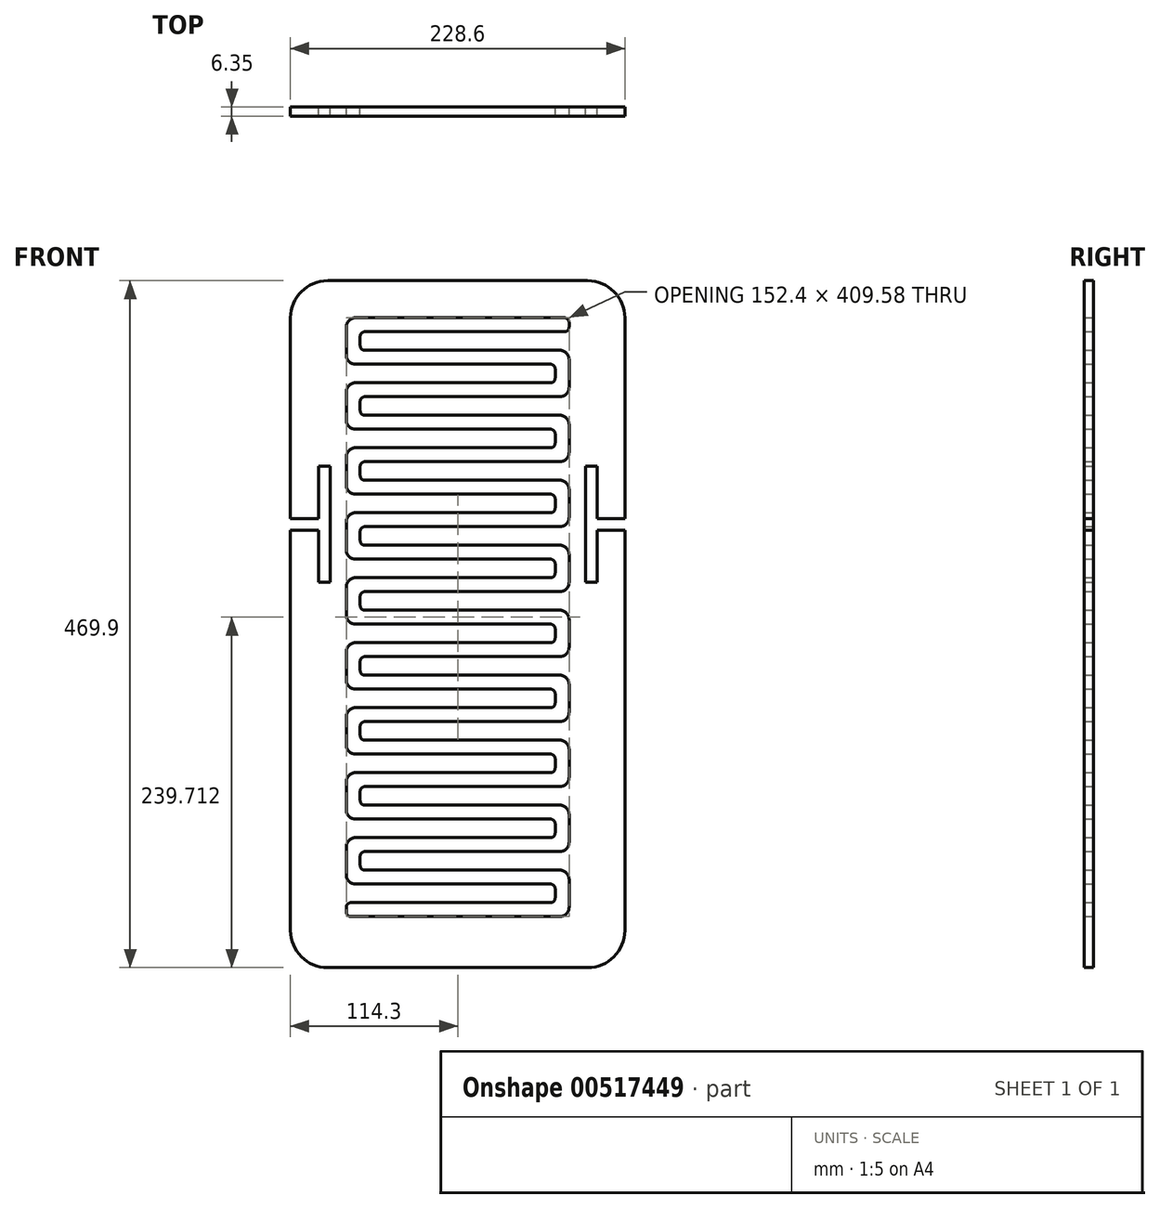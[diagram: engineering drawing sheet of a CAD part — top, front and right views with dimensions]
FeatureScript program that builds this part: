
annotation { "Feature Type Name" : "Feature", "Feature Type Description" : "" }
export const myFeature = defineFeature(function(context is Context, id is Id, definition is map)
    precondition{}
    {
        {
            var Q0;
            Q0=qCreatedBy(makeId("Front.planeOp"),FACE);
            var sketch = newSketch(context, id + "F0", { "sketchPlane" : qUnion([Q0])});
            skLineSegment(sketch, "E0.bottom", {"start": v(88.9, -234.95) * mm, "end": v(-88.9, -234.95) * mm});
            skLineSegment(sketch, "E0.top", {"start": v(88.9, 234.95) * mm, "end": v(-88.9, 234.95) * mm});
            skLineSegment(sketch, "E0.left", {"start": v(114.3, -209.55) * mm, "end": v(114.3, 209.55) * mm});
            skLineSegment(sketch, "E0.right", {"start": v(-114.3, -209.55) * mm, "end": v(-114.3, 209.55) * mm});
            skPoint(sketch, "E0.middle", {"position": v(0, 0) * mm});
            skPoint(sketch, "E1.visualSharp", {"position": v(-114.3, 234.95) * mm});
            skArc(sketch, "E1.filletArc", {"start": v(-88.9, 234.95) * mm, "mid": v(-106.86, 227.51) * mm, "end": v(-114.3, 209.55) * mm});
            skPoint(sketch, "E2.visualSharp", {"position": v(114.3, 234.95) * mm});
            skArc(sketch, "E2.filletArc", {"start": v(114.3, 209.55) * mm, "mid": v(106.86, 227.51) * mm, "end": v(88.9, 234.95) * mm});
            skPoint(sketch, "E3.visualSharp", {"position": v(114.3, -234.95) * mm});
            skArc(sketch, "E3.filletArc", {"start": v(88.9, -234.95) * mm, "mid": v(106.86, -227.51) * mm, "end": v(114.3, -209.55) * mm});
            skPoint(sketch, "E4.visualSharp", {"position": v(-114.3, -234.95) * mm});
            skArc(sketch, "E4.filletArc", {"start": v(-114.3, -209.55) * mm, "mid": v(-106.86, -227.51) * mm, "end": v(-88.9, -234.95) * mm});
            skLineSegment(sketch, "E5.bottom", {"start": v(-95.25, 107.95) * mm, "end": v(-87.31, 107.95) * mm});
            skLineSegment(sketch, "E5.top", {"start": v(-95.25, 28.57) * mm, "end": v(-87.31, 28.57) * mm});
            skLineSegment(sketch, "E5.left", {"start": v(-95.25, 107.95) * mm, "end": v(-95.25, 28.57) * mm});
            skLineSegment(sketch, "E5.right", {"start": v(-87.31, 107.95) * mm, "end": v(-87.31, 28.57) * mm});
            skLineSegment(sketch, "E6.MirrorCS", {"start": v(95.25, 107.95) * mm, "end": v(87.31, 107.95) * mm});
            skLineSegment(sketch, "E7.MirrorCS", {"start": v(95.25, 28.58) * mm, "end": v(87.31, 28.58) * mm});
            skLineSegment(sketch, "E8.MirrorCS", {"start": v(87.31, 107.95) * mm, "end": v(87.31, 28.57) * mm});
            skLineSegment(sketch, "E9.MirrorCS", {"start": v(95.25, 107.95) * mm, "end": v(95.25, 28.57) * mm});
            skLineSegment(sketch, "E10", {"start": v(-69.85, 209.55) * mm, "end": v(73.02, 209.55) * mm});
            skLineSegment(sketch, "E11", {"start": v(76.2, 206.38) * mm, "end": v(76.2, 203.2) * mm});
            skLineSegment(sketch, "E12", {"start": v(73.02, 200.03) * mm, "end": v(-63.5, 200.03) * mm});
            skLineSegment(sketch, "E13", {"start": v(-66.68, 196.85) * mm, "end": v(-66.68, 190.5) * mm});
            skLineSegment(sketch, "E14", {"start": v(-63.5, 187.33) * mm, "end": v(69.85, 187.33) * mm});
            skLineSegment(sketch, "E15", {"start": v(76.2, 180.98) * mm, "end": v(76.2, 161.93) * mm});
            skLineSegment(sketch, "E16", {"start": v(-76.2, 203.2) * mm, "end": v(-76.2, 184.15) * mm});
            skLineSegment(sketch, "E17", {"start": v(-69.85, 177.8) * mm, "end": v(63.5, 177.8) * mm});
            skLineSegment(sketch, "E18", {"start": v(66.67, 174.63) * mm, "end": v(66.67, 168.28) * mm});
            skLineSegment(sketch, "E19", {"start": v(63.5, 165.1) * mm, "end": v(-69.85, 165.1) * mm});
            skPoint(sketch, "E20.visualSharp", {"position": v(-76.2, 209.55) * mm});
            skArc(sketch, "E20.filletArc", {"start": v(-69.85, 209.55) * mm, "mid": v(-74.34, 207.7) * mm, "end": v(-76.2, 203.2) * mm});
            skPoint(sketch, "E21.visualSharp", {"position": v(-66.68, 200.03) * mm});
            skArc(sketch, "E21.filletArc", {"start": v(-63.5, 200.03) * mm, "mid": v(-65.75, 199.1) * mm, "end": v(-66.68, 196.85) * mm});
            skPoint(sketch, "E22.visualSharp", {"position": v(-66.68, 187.33) * mm});
            skArc(sketch, "E22.filletArc", {"start": v(-66.68, 190.5) * mm, "mid": v(-65.75, 188.25) * mm, "end": v(-63.5, 187.33) * mm});
            skPoint(sketch, "E23.visualSharp", {"position": v(-76.2, 177.8) * mm});
            skArc(sketch, "E23.filletArc", {"start": v(-76.2, 184.15) * mm, "mid": v(-74.34, 179.66) * mm, "end": v(-69.85, 177.8) * mm});
            skPoint(sketch, "E24.visualSharp", {"position": v(76.2, 187.33) * mm});
            skArc(sketch, "E24.filletArc", {"start": v(76.2, 180.98) * mm, "mid": v(74.34, 185.47) * mm, "end": v(69.85, 187.33) * mm});
            skPoint(sketch, "E25.visualSharp", {"position": v(76.2, 200.03) * mm});
            skArc(sketch, "E25.filletArc", {"start": v(73.02, 200.03) * mm, "mid": v(75.27, 200.95) * mm, "end": v(76.2, 203.2) * mm});
            skPoint(sketch, "E26.visualSharp", {"position": v(76.2, 209.55) * mm});
            skArc(sketch, "E26.filletArc", {"start": v(76.2, 206.38) * mm, "mid": v(75.27, 208.62) * mm, "end": v(73.02, 209.55) * mm});
            skPoint(sketch, "E27.visualSharp", {"position": v(66.67, 177.8) * mm});
            skArc(sketch, "E27.filletArc", {"start": v(66.67, 174.63) * mm, "mid": v(65.75, 176.87) * mm, "end": v(63.5, 177.8) * mm});
            skPoint(sketch, "E28.visualSharp", {"position": v(66.67, 165.1) * mm});
            skArc(sketch, "E28.filletArc", {"start": v(63.5, 165.1) * mm, "mid": v(65.75, 166.03) * mm, "end": v(66.67, 168.28) * mm});
            skArc(sketch, "E29.filletArc", {"start": v(69.85, 155.58) * mm, "mid": v(74.34, 157.43) * mm, "end": v(76.2, 161.93) * mm});
            skPoint(sketch, "E30.visualSharp", {"position": v(-76.2, 165.1) * mm});
            skLineSegment(sketch, "E31", {"start": v(69.85, 155.58) * mm, "end": v(-63.5, 155.58) * mm});
            skLineSegment(sketch, "E32.0.1.0", {"start": v(69.85, 111.13) * mm, "end": v(-63.5, 111.13) * mm});
            skLineSegment(sketch, "E32.0.1.1", {"start": v(63.5, 120.65) * mm, "end": v(-69.85, 120.65) * mm});
            skArc(sketch, "E32.0.1.2", {"start": v(69.85, 111.13) * mm, "mid": v(74.34, 112.98) * mm, "end": v(76.2, 117.48) * mm});
            skLineSegment(sketch, "E32.0.1.3", {"start": v(76.2, 136.53) * mm, "end": v(76.2, 117.48) * mm});
            skArc(sketch, "E32.0.1.4", {"start": v(63.5, 120.65) * mm, "mid": v(65.75, 121.58) * mm, "end": v(66.67, 123.83) * mm});
            skLineSegment(sketch, "E32.0.1.5", {"start": v(66.67, 130.18) * mm, "end": v(66.67, 123.83) * mm});
            skArc(sketch, "E32.0.1.6", {"start": v(66.67, 130.18) * mm, "mid": v(65.75, 132.42) * mm, "end": v(63.5, 133.35) * mm});
            skArc(sketch, "E32.0.1.7", {"start": v(76.2, 136.53) * mm, "mid": v(74.34, 141.02) * mm, "end": v(69.85, 142.88) * mm});
            skLineSegment(sketch, "E32.0.1.8", {"start": v(-63.5, 142.88) * mm, "end": v(69.85, 142.88) * mm});
            skLineSegment(sketch, "E32.0.1.9", {"start": v(-69.85, 133.35) * mm, "end": v(63.5, 133.35) * mm});
            skArc(sketch, "E32.0.1.10", {"start": v(-76.2, 139.7) * mm, "mid": v(-74.34, 135.2) * mm, "end": v(-69.85, 133.35) * mm});
            skLineSegment(sketch, "E32.0.1.11", {"start": v(-76.2, 158.75) * mm, "end": v(-76.2, 139.7) * mm});
            skArc(sketch, "E32.0.1.12", {"start": v(-69.85, 165.1) * mm, "mid": v(-74.34, 163.24) * mm, "end": v(-76.2, 158.75) * mm});
            skArc(sketch, "E32.0.1.13", {"start": v(-63.5, 155.57) * mm, "mid": v(-65.75, 154.65) * mm, "end": v(-66.68, 152.4) * mm});
            skLineSegment(sketch, "E32.0.1.14", {"start": v(-66.68, 152.4) * mm, "end": v(-66.68, 146.05) * mm});
            skArc(sketch, "E32.0.1.15", {"start": v(-66.68, 146.05) * mm, "mid": v(-65.75, 143.8) * mm, "end": v(-63.5, 142.88) * mm});
            skLineSegment(sketch, "E32.direction1", {"start": v(-63.5, 155.58) * mm, "end": v(-38.1, 155.58) * mm, "construction": true});
            skLineSegment(sketch, "E32.direction2", {"start": v(-63.5, 155.58) * mm, "end": v(-63.5, 111.13) * mm, "construction": true});
            skLineSegment(sketch, "E33.0.0.2", {"start": v(69.85, 66.68) * mm, "end": v(-63.5, 66.68) * mm});
            skLineSegment(sketch, "E33.3.0.2", {"start": v(63.5, 76.2) * mm, "end": v(-69.85, 76.2) * mm});
            skArc(sketch, "E33.6.0.2", {"start": v(69.85, 66.68) * mm, "mid": v(74.34, 68.53) * mm, "end": v(76.2, 73.03) * mm});
            skLineSegment(sketch, "E33.10.0.2", {"start": v(76.2, 92.08) * mm, "end": v(76.2, 73.03) * mm});
            skArc(sketch, "E33.13.0.2", {"start": v(63.5, 76.2) * mm, "mid": v(65.75, 77.13) * mm, "end": v(66.67, 79.38) * mm});
            skLineSegment(sketch, "E33.17.0.2", {"start": v(66.67, 85.73) * mm, "end": v(66.67, 79.38) * mm});
            skArc(sketch, "E33.20.0.2", {"start": v(66.67, 85.73) * mm, "mid": v(65.75, 87.97) * mm, "end": v(63.5, 88.9) * mm});
            skArc(sketch, "E33.24.0.2", {"start": v(76.2, 92.08) * mm, "mid": v(74.34, 96.57) * mm, "end": v(69.85, 98.43) * mm});
            skLineSegment(sketch, "E33.28.0.2", {"start": v(-63.5, 98.43) * mm, "end": v(69.85, 98.43) * mm});
            skLineSegment(sketch, "E33.31.0.2", {"start": v(-69.85, 88.9) * mm, "end": v(63.5, 88.9) * mm});
            skArc(sketch, "E33.34.0.2", {"start": v(-76.2, 95.25) * mm, "mid": v(-74.34, 90.76) * mm, "end": v(-69.85, 88.9) * mm});
            skLineSegment(sketch, "E33.38.0.2", {"start": v(-76.2, 114.3) * mm, "end": v(-76.2, 95.25) * mm});
            skArc(sketch, "E33.41.0.2", {"start": v(-69.85, 120.65) * mm, "mid": v(-74.34, 118.8) * mm, "end": v(-76.2, 114.3) * mm});
            skArc(sketch, "E33.45.0.2", {"start": v(-63.5, 111.12) * mm, "mid": v(-65.75, 110.2) * mm, "end": v(-66.68, 107.95) * mm});
            skLineSegment(sketch, "E33.49.0.2", {"start": v(-66.68, 107.95) * mm, "end": v(-66.68, 101.6) * mm});
            skArc(sketch, "E33.52.0.2", {"start": v(-66.68, 101.6) * mm, "mid": v(-65.75, 99.35) * mm, "end": v(-63.5, 98.43) * mm});
            skLineSegment(sketch, "E33.0.0.3", {"start": v(69.85, 22.23) * mm, "end": v(-63.5, 22.23) * mm});
            skLineSegment(sketch, "E33.3.0.3", {"start": v(63.5, 31.75) * mm, "end": v(-69.85, 31.75) * mm});
            skArc(sketch, "E33.6.0.3", {"start": v(69.85, 22.23) * mm, "mid": v(74.34, 24.08) * mm, "end": v(76.2, 28.58) * mm});
            skLineSegment(sketch, "E33.10.0.3", {"start": v(76.2, 47.63) * mm, "end": v(76.2, 28.58) * mm});
            skArc(sketch, "E33.13.0.3", {"start": v(63.5, 31.75) * mm, "mid": v(65.75, 32.68) * mm, "end": v(66.67, 34.93) * mm});
            skLineSegment(sketch, "E33.17.0.3", {"start": v(66.67, 41.28) * mm, "end": v(66.67, 34.93) * mm});
            skArc(sketch, "E33.20.0.3", {"start": v(66.67, 41.28) * mm, "mid": v(65.75, 43.52) * mm, "end": v(63.5, 44.45) * mm});
            skArc(sketch, "E33.24.0.3", {"start": v(76.2, 47.63) * mm, "mid": v(74.34, 52.12) * mm, "end": v(69.85, 53.98) * mm});
            skLineSegment(sketch, "E33.28.0.3", {"start": v(-63.5, 53.98) * mm, "end": v(69.85, 53.98) * mm});
            skLineSegment(sketch, "E33.31.0.3", {"start": v(-69.85, 44.45) * mm, "end": v(63.5, 44.45) * mm});
            skArc(sketch, "E33.34.0.3", {"start": v(-76.2, 50.8) * mm, "mid": v(-74.34, 46.3) * mm, "end": v(-69.85, 44.45) * mm});
            skLineSegment(sketch, "E33.38.0.3", {"start": v(-76.2, 69.85) * mm, "end": v(-76.2, 50.8) * mm});
            skArc(sketch, "E33.41.0.3", {"start": v(-69.85, 76.2) * mm, "mid": v(-74.34, 74.34) * mm, "end": v(-76.2, 69.85) * mm});
            skArc(sketch, "E33.45.0.3", {"start": v(-63.5, 66.67) * mm, "mid": v(-65.75, 65.75) * mm, "end": v(-66.68, 63.5) * mm});
            skLineSegment(sketch, "E33.49.0.3", {"start": v(-66.68, 63.5) * mm, "end": v(-66.68, 57.15) * mm});
            skArc(sketch, "E33.52.0.3", {"start": v(-66.68, 57.15) * mm, "mid": v(-65.75, 54.9) * mm, "end": v(-63.5, 53.98) * mm});
            skLineSegment(sketch, "E33.0.0.4", {"start": v(69.85, -22.22) * mm, "end": v(-63.5, -22.22) * mm});
            skLineSegment(sketch, "E33.3.0.4", {"start": v(63.5, -12.7) * mm, "end": v(-69.85, -12.7) * mm});
            skArc(sketch, "E33.6.0.4", {"start": v(69.85, -22.22) * mm, "mid": v(74.34, -20.37) * mm, "end": v(76.2, -15.87) * mm});
            skLineSegment(sketch, "E33.10.0.4", {"start": v(76.2, 3.18) * mm, "end": v(76.2, -15.87) * mm});
            skArc(sketch, "E33.13.0.4", {"start": v(63.5, -12.7) * mm, "mid": v(65.75, -11.77) * mm, "end": v(66.67, -9.52) * mm});
            skLineSegment(sketch, "E33.17.0.4", {"start": v(66.67, -3.17) * mm, "end": v(66.67, -9.52) * mm});
            skArc(sketch, "E33.20.0.4", {"start": v(66.67, -3.17) * mm, "mid": v(65.75, -0.93) * mm, "end": v(63.5, 0) * mm});
            skArc(sketch, "E33.24.0.4", {"start": v(76.2, 3.18) * mm, "mid": v(74.34, 7.67) * mm, "end": v(69.85, 9.53) * mm});
            skLineSegment(sketch, "E33.28.0.4", {"start": v(-63.5, 9.53) * mm, "end": v(69.85, 9.53) * mm});
            skLineSegment(sketch, "E33.31.0.4", {"start": v(-69.85, 0) * mm, "end": v(63.5, 0) * mm});
            skArc(sketch, "E33.34.0.4", {"start": v(-76.2, 6.35) * mm, "mid": v(-74.34, 1.86) * mm, "end": v(-69.85, 0) * mm});
            skLineSegment(sketch, "E33.38.0.4", {"start": v(-76.2, 25.4) * mm, "end": v(-76.2, 6.35) * mm});
            skArc(sketch, "E33.41.0.4", {"start": v(-69.85, 31.75) * mm, "mid": v(-74.34, 29.9) * mm, "end": v(-76.2, 25.4) * mm});
            skArc(sketch, "E33.45.0.4", {"start": v(-63.5, 22.22) * mm, "mid": v(-65.75, 21.3) * mm, "end": v(-66.68, 19.05) * mm});
            skLineSegment(sketch, "E33.49.0.4", {"start": v(-66.68, 19.05) * mm, "end": v(-66.68, 12.7) * mm});
            skArc(sketch, "E33.52.0.4", {"start": v(-66.68, 12.7) * mm, "mid": v(-65.75, 10.45) * mm, "end": v(-63.5, 9.53) * mm});
            skLineSegment(sketch, "E33.0.0.5", {"start": v(69.85, -66.67) * mm, "end": v(-63.5, -66.67) * mm});
            skLineSegment(sketch, "E33.3.0.5", {"start": v(63.5, -57.15) * mm, "end": v(-69.85, -57.15) * mm});
            skArc(sketch, "E33.6.0.5", {"start": v(69.85, -66.67) * mm, "mid": v(74.34, -64.82) * mm, "end": v(76.2, -60.32) * mm});
            skLineSegment(sketch, "E33.10.0.5", {"start": v(76.2, -41.27) * mm, "end": v(76.2, -60.32) * mm});
            skArc(sketch, "E33.13.0.5", {"start": v(63.5, -57.15) * mm, "mid": v(65.75, -56.22) * mm, "end": v(66.67, -53.97) * mm});
            skLineSegment(sketch, "E33.17.0.5", {"start": v(66.67, -47.62) * mm, "end": v(66.67, -53.97) * mm});
            skArc(sketch, "E33.20.0.5", {"start": v(66.67, -47.62) * mm, "mid": v(65.75, -45.38) * mm, "end": v(63.5, -44.45) * mm});
            skArc(sketch, "E33.24.0.5", {"start": v(76.2, -41.27) * mm, "mid": v(74.34, -36.78) * mm, "end": v(69.85, -34.92) * mm});
            skLineSegment(sketch, "E33.28.0.5", {"start": v(-63.5, -34.92) * mm, "end": v(69.85, -34.92) * mm});
            skLineSegment(sketch, "E33.31.0.5", {"start": v(-69.85, -44.45) * mm, "end": v(63.5, -44.45) * mm});
            skArc(sketch, "E33.34.0.5", {"start": v(-76.2, -38.1) * mm, "mid": v(-74.34, -42.6) * mm, "end": v(-69.85, -44.45) * mm});
            skLineSegment(sketch, "E33.38.0.5", {"start": v(-76.2, -19.05) * mm, "end": v(-76.2, -38.1) * mm});
            skArc(sketch, "E33.41.0.5", {"start": v(-69.85, -12.7) * mm, "mid": v(-74.34, -14.56) * mm, "end": v(-76.2, -19.05) * mm});
            skArc(sketch, "E33.45.0.5", {"start": v(-63.5, -22.23) * mm, "mid": v(-65.75, -23.15) * mm, "end": v(-66.68, -25.4) * mm});
            skLineSegment(sketch, "E33.49.0.5", {"start": v(-66.68, -25.4) * mm, "end": v(-66.68, -31.75) * mm});
            skArc(sketch, "E33.52.0.5", {"start": v(-66.68, -31.75) * mm, "mid": v(-65.75, -34) * mm, "end": v(-63.5, -34.92) * mm});
            skLineSegment(sketch, "E33.0.0.6", {"start": v(69.85, -111.12) * mm, "end": v(-63.5, -111.12) * mm});
            skLineSegment(sketch, "E33.3.0.6", {"start": v(63.5, -101.6) * mm, "end": v(-69.85, -101.6) * mm});
            skArc(sketch, "E33.6.0.6", {"start": v(69.85, -111.12) * mm, "mid": v(74.34, -109.27) * mm, "end": v(76.2, -104.77) * mm});
            skLineSegment(sketch, "E33.10.0.6", {"start": v(76.2, -85.72) * mm, "end": v(76.2, -104.77) * mm});
            skArc(sketch, "E33.13.0.6", {"start": v(63.5, -101.6) * mm, "mid": v(65.75, -100.67) * mm, "end": v(66.67, -98.42) * mm});
            skLineSegment(sketch, "E33.17.0.6", {"start": v(66.67, -92.07) * mm, "end": v(66.67, -98.42) * mm});
            skArc(sketch, "E33.20.0.6", {"start": v(66.67, -92.07) * mm, "mid": v(65.75, -89.83) * mm, "end": v(63.5, -88.9) * mm});
            skArc(sketch, "E33.24.0.6", {"start": v(76.2, -85.72) * mm, "mid": v(74.34, -81.23) * mm, "end": v(69.85, -79.37) * mm});
            skLineSegment(sketch, "E33.28.0.6", {"start": v(-63.5, -79.37) * mm, "end": v(69.85, -79.37) * mm});
            skLineSegment(sketch, "E33.31.0.6", {"start": v(-69.85, -88.9) * mm, "end": v(63.5, -88.9) * mm});
            skArc(sketch, "E33.34.0.6", {"start": v(-76.2, -82.55) * mm, "mid": v(-74.34, -87.04) * mm, "end": v(-69.85, -88.9) * mm});
            skLineSegment(sketch, "E33.38.0.6", {"start": v(-76.2, -63.5) * mm, "end": v(-76.2, -82.55) * mm});
            skArc(sketch, "E33.41.0.6", {"start": v(-69.85, -57.15) * mm, "mid": v(-74.34, -59) * mm, "end": v(-76.2, -63.5) * mm});
            skArc(sketch, "E33.45.0.6", {"start": v(-63.5, -66.68) * mm, "mid": v(-65.75, -67.6) * mm, "end": v(-66.68, -69.85) * mm});
            skLineSegment(sketch, "E33.49.0.6", {"start": v(-66.68, -69.85) * mm, "end": v(-66.68, -76.2) * mm});
            skArc(sketch, "E33.52.0.6", {"start": v(-66.68, -76.2) * mm, "mid": v(-65.75, -78.45) * mm, "end": v(-63.5, -79.38) * mm});
            skLineSegment(sketch, "E33.0.0.7", {"start": v(69.85, -155.57) * mm, "end": v(-63.5, -155.57) * mm});
            skLineSegment(sketch, "E33.3.0.7", {"start": v(63.5, -146.05) * mm, "end": v(-69.85, -146.05) * mm});
            skArc(sketch, "E33.6.0.7", {"start": v(69.85, -155.57) * mm, "mid": v(74.34, -153.72) * mm, "end": v(76.2, -149.22) * mm});
            skLineSegment(sketch, "E33.10.0.7", {"start": v(76.2, -130.17) * mm, "end": v(76.2, -149.22) * mm});
            skArc(sketch, "E33.13.0.7", {"start": v(63.5, -146.05) * mm, "mid": v(65.75, -145.12) * mm, "end": v(66.67, -142.87) * mm});
            skLineSegment(sketch, "E33.17.0.7", {"start": v(66.67, -136.52) * mm, "end": v(66.67, -142.87) * mm});
            skArc(sketch, "E33.20.0.7", {"start": v(66.67, -136.52) * mm, "mid": v(65.75, -134.28) * mm, "end": v(63.5, -133.35) * mm});
            skArc(sketch, "E33.24.0.7", {"start": v(76.2, -130.17) * mm, "mid": v(74.34, -125.68) * mm, "end": v(69.85, -123.82) * mm});
            skLineSegment(sketch, "E33.28.0.7", {"start": v(-63.5, -123.82) * mm, "end": v(69.85, -123.82) * mm});
            skLineSegment(sketch, "E33.31.0.7", {"start": v(-69.85, -133.35) * mm, "end": v(63.5, -133.35) * mm});
            skArc(sketch, "E33.34.0.7", {"start": v(-76.2, -127) * mm, "mid": v(-74.34, -131.5) * mm, "end": v(-69.85, -133.35) * mm});
            skLineSegment(sketch, "E33.38.0.7", {"start": v(-76.2, -107.95) * mm, "end": v(-76.2, -127) * mm});
            skArc(sketch, "E33.41.0.7", {"start": v(-69.85, -101.6) * mm, "mid": v(-74.34, -103.46) * mm, "end": v(-76.2, -107.95) * mm});
            skArc(sketch, "E33.45.0.7", {"start": v(-63.5, -111.13) * mm, "mid": v(-65.75, -112.05) * mm, "end": v(-66.68, -114.3) * mm});
            skLineSegment(sketch, "E33.49.0.7", {"start": v(-66.68, -114.3) * mm, "end": v(-66.68, -120.65) * mm});
            skArc(sketch, "E33.52.0.7", {"start": v(-66.68, -120.65) * mm, "mid": v(-65.75, -122.9) * mm, "end": v(-63.5, -123.83) * mm});
            skPoint(sketch, "E34.visualSharp", {"position": v(120.65, -352.42) * mm});
            skArc(sketch, "E34.filletArc", {"start": v(120.65, -355.6) * mm, "mid": v(119.72, -353.35) * mm, "end": v(117.47, -352.42) * mm});
            skPoint(sketch, "E35.visualSharp", {"position": v(120.65, -361.95) * mm});
            skArc(sketch, "E35.filletArc", {"start": v(117.47, -361.95) * mm, "mid": v(119.72, -361.02) * mm, "end": v(120.65, -358.77) * mm});
            skLineSegment(sketch, "E36", {"start": v(-95.25, 68.26) * mm, "end": v(-114.3, 68.26) * mm, "construction": true});
            skLineSegment(sketch, "E37.bottom", {"start": v(-114.3, 72.23) * mm, "end": v(-95.25, 72.23) * mm});
            skLineSegment(sketch, "E37.top", {"start": v(-114.3, 64.3) * mm, "end": v(-95.25, 64.3) * mm});
            skLineSegment(sketch, "E37.left", {"start": v(-114.3, 72.23) * mm, "end": v(-114.3, 64.3) * mm});
            skLineSegment(sketch, "E37.right", {"start": v(-95.25, 72.23) * mm, "end": v(-95.25, 64.3) * mm});
            skLineSegment(sketch, "E38.MirrorCS", {"start": v(-95.25, 64.3) * mm, "end": v(-95.25, 72.23) * mm});
            skLineSegment(sketch, "E39.MirrorCS", {"start": v(-114.3, 64.3) * mm, "end": v(-114.3, 72.23) * mm});
            skLineSegment(sketch, "E40.MirrorCS", {"start": v(114.3, 72.23) * mm, "end": v(114.3, 64.3) * mm});
            skLineSegment(sketch, "E41.MirrorCS", {"start": v(95.25, 72.23) * mm, "end": v(95.25, 64.3) * mm});
            skLineSegment(sketch, "E42.MirrorCS", {"start": v(114.3, 72.23) * mm, "end": v(95.25, 72.23) * mm});
            skLineSegment(sketch, "E43.MirrorCS", {"start": v(114.3, 64.3) * mm, "end": v(95.25, 64.3) * mm});
            skLineSegment(sketch, "E44.MirrorCS", {"start": v(95.25, 64.3) * mm, "end": v(95.25, 72.23) * mm});
            skLineSegment(sketch, "E45.MirrorCS", {"start": v(114.3, 64.3) * mm, "end": v(114.3, 72.23) * mm});
            skLineSegment(sketch, "E46.MirrorCS", {"start": v(95.25, 68.26) * mm, "end": v(114.3, 68.26) * mm, "construction": true});
            skLineSegment(sketch, "E47.0.0.8", {"start": v(69.85, -200.02) * mm, "end": v(-63.5, -200.02) * mm});
            skLineSegment(sketch, "E47.3.0.8", {"start": v(63.5, -190.5) * mm, "end": v(-69.85, -190.5) * mm});
            skArc(sketch, "E47.6.0.8", {"start": v(69.85, -200.02) * mm, "mid": v(74.34, -198.17) * mm, "end": v(76.2, -193.67) * mm});
            skLineSegment(sketch, "E47.10.0.8", {"start": v(76.2, -174.62) * mm, "end": v(76.2, -193.67) * mm});
            skArc(sketch, "E47.13.0.8", {"start": v(63.5, -190.5) * mm, "mid": v(65.75, -189.57) * mm, "end": v(66.67, -187.32) * mm});
            skLineSegment(sketch, "E47.17.0.8", {"start": v(66.67, -180.97) * mm, "end": v(66.67, -187.32) * mm});
            skArc(sketch, "E47.20.0.8", {"start": v(66.67, -180.97) * mm, "mid": v(65.75, -178.73) * mm, "end": v(63.5, -177.8) * mm});
            skArc(sketch, "E47.24.0.8", {"start": v(76.2, -174.62) * mm, "mid": v(74.34, -170.13) * mm, "end": v(69.85, -168.27) * mm});
            skLineSegment(sketch, "E47.28.0.8", {"start": v(-63.5, -168.27) * mm, "end": v(69.85, -168.27) * mm});
            skLineSegment(sketch, "E47.31.0.8", {"start": v(-69.85, -177.8) * mm, "end": v(63.5, -177.8) * mm});
            skArc(sketch, "E47.34.0.8", {"start": v(-76.2, -171.45) * mm, "mid": v(-74.34, -175.94) * mm, "end": v(-69.85, -177.8) * mm});
            skLineSegment(sketch, "E47.38.0.8", {"start": v(-76.2, -152.4) * mm, "end": v(-76.2, -171.45) * mm});
            skArc(sketch, "E47.41.0.8", {"start": v(-69.85, -146.05) * mm, "mid": v(-74.34, -147.9) * mm, "end": v(-76.2, -152.4) * mm});
            skArc(sketch, "E47.45.0.8", {"start": v(-63.5, -155.58) * mm, "mid": v(-65.75, -156.5) * mm, "end": v(-66.68, -158.75) * mm});
            skLineSegment(sketch, "E47.49.0.8", {"start": v(-66.68, -158.75) * mm, "end": v(-66.68, -165.1) * mm});
            skArc(sketch, "E47.52.0.8", {"start": v(-66.68, -165.1) * mm, "mid": v(-65.75, -167.35) * mm, "end": v(-63.5, -168.28) * mm});
            skLineSegment(sketch, "E48", {"start": v(-63.5, -200.02) * mm, "end": v(-73.03, -200.02) * mm});
            skLineSegment(sketch, "E49", {"start": v(-69.85, -190.5) * mm, "end": v(-73.03, -190.5) * mm});
            skLineSegment(sketch, "E50", {"start": v(-76.2, -193.67) * mm, "end": v(-76.2, -196.85) * mm});
            skPoint(sketch, "E51.visualSharp", {"position": v(-76.2, -190.5) * mm});
            skArc(sketch, "E51.filletArc", {"start": v(-73.03, -190.5) * mm, "mid": v(-75.27, -191.43) * mm, "end": v(-76.2, -193.67) * mm});
            skPoint(sketch, "E52.visualSharp", {"position": v(-76.2, -200.02) * mm});
            skArc(sketch, "E52.filletArc", {"start": v(-76.2, -196.85) * mm, "mid": v(-75.27, -199.1) * mm, "end": v(-73.03, -200.03) * mm});
            skSolve(sketch);
        }
        {
            var Q0;
            Q0=makeQuery(id+"F0.imprint","IMPRINT",FACE,{"disambiguationData":[TD([[makeQuery(id+"F0.imprint","IMPRINT",EDGE,{"derivedFrom":sQuery(id+"F0.wireOp",EDGE,"E0.bottom")}),-1.0]])]});
            extrude(context, id + "F1", {"entities" : qUnion([Q0]), "depth" : 6.35 * mm, "offsetDistance" : 25.4 * mm});
        }
    });
